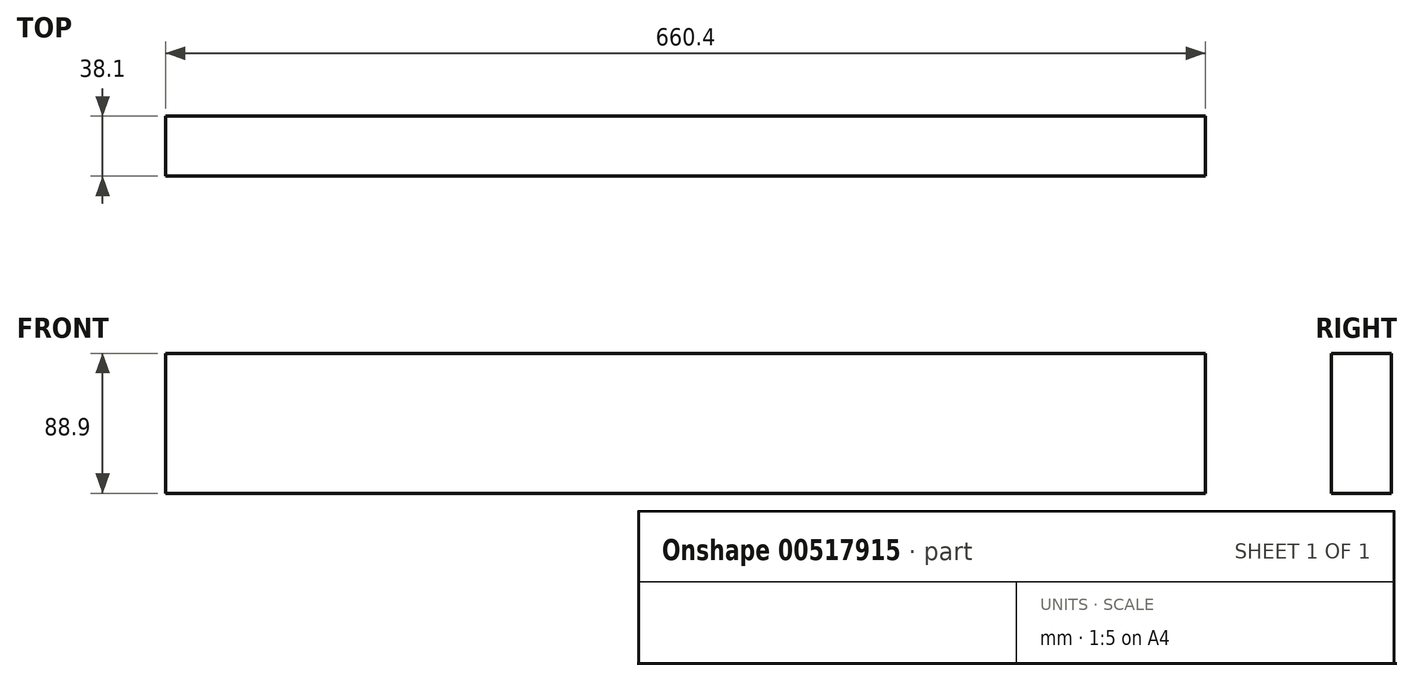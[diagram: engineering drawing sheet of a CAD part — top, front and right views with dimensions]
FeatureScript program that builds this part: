
annotation { "Feature Type Name" : "Feature", "Feature Type Description" : "" }
export const myFeature = defineFeature(function(context is Context, id is Id, definition is map)
    precondition{}
    {
        {
            var Q0;
            Q0=qCreatedBy(makeId("Right.planeOp"),FACE);
            var sketch = newSketch(context, id + "F0", { "sketchPlane" : qUnion([Q0])});
            skLineSegment(sketch, "E0.bottom", {"start": v(19.05, 44.45) * mm, "end": v(-19.05, 44.45) * mm});
            skLineSegment(sketch, "E0.top", {"start": v(19.05, -44.45) * mm, "end": v(-19.05, -44.45) * mm});
            skLineSegment(sketch, "E0.left", {"start": v(19.05, 44.45) * mm, "end": v(19.05, -44.45) * mm});
            skLineSegment(sketch, "E0.right", {"start": v(-19.05, 44.45) * mm, "end": v(-19.05, -44.45) * mm});
            skPoint(sketch, "E0.middle", {"position": v(0, 0) * mm});
            skSolve(sketch);
        }
        {
            var Q0;
            Q0=makeQuery(id+"F0.imprint","IMPRINT",FACE,{"disambiguationData":[TD([[makeQuery(id+"F0.imprint","IMPRINT",EDGE,{"derivedFrom":sQuery(id+"F0.wireOp",EDGE,"E0.bottom")}),1.0]])]});
            extrude(context, id + "F1", {"entities" : qUnion([Q0]), "endBound" : BoundingType.SYMMETRIC, "depth" : 660.4 * mm, "offsetDistance" : 25.4 * mm});
        }
    });
